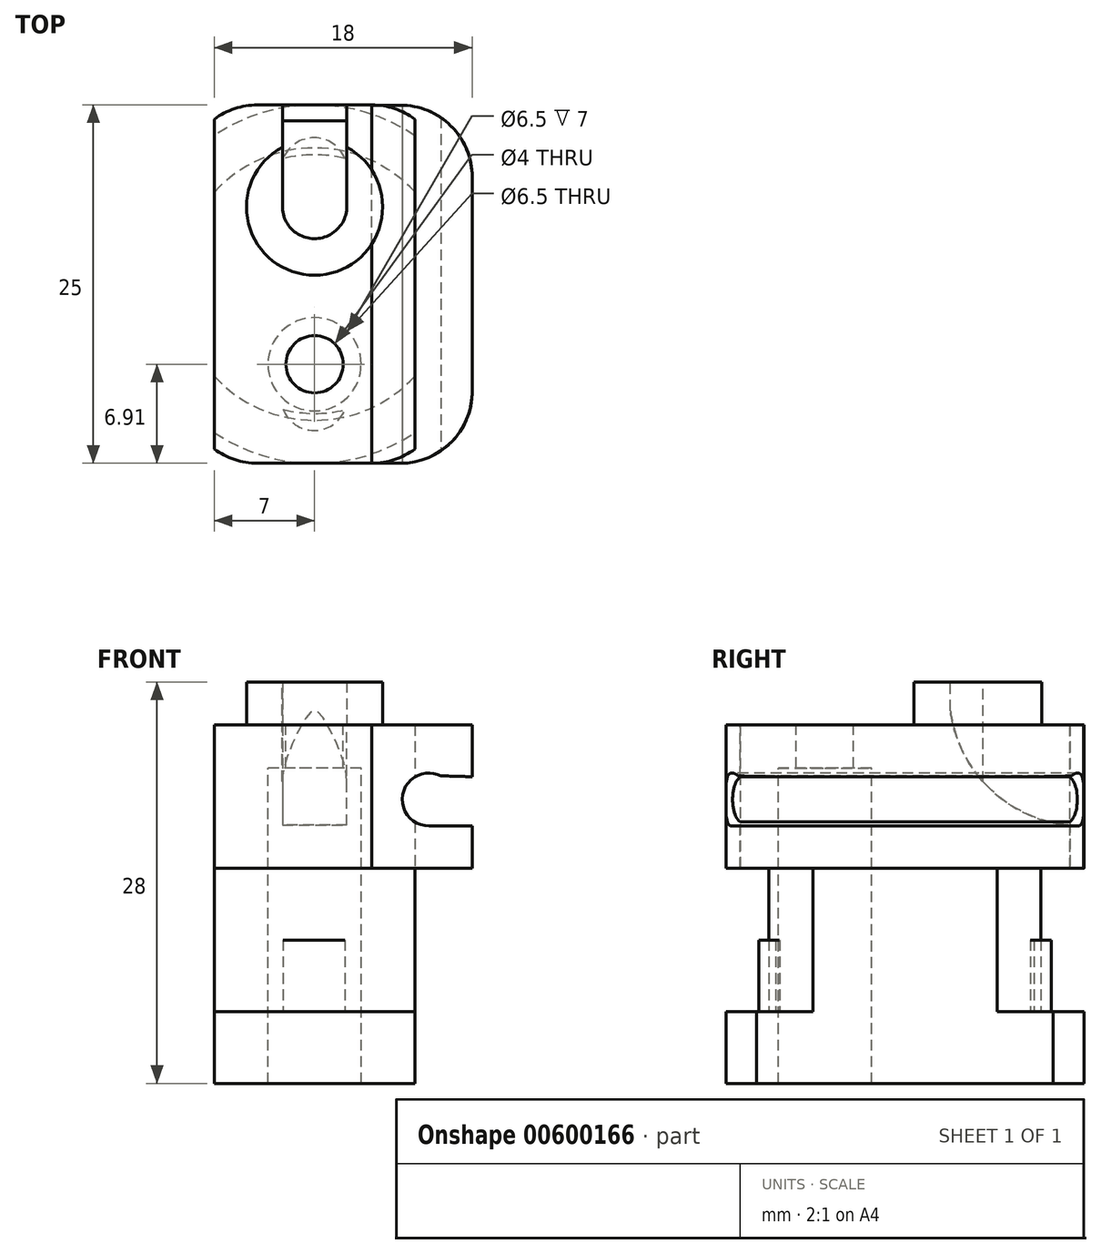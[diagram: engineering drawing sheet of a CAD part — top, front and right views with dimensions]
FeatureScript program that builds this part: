
annotation { "Feature Type Name" : "Feature", "Feature Type Description" : "" }
export const myFeature = defineFeature(function(context is Context, id is Id, definition is map)
    precondition{}
    {
        {
            var Q0;
            Q0=qCreatedBy(makeId("Top.planeOp"),FACE);
            var sketch = newSketch(context, id + "F0", { "sketchPlane" : qUnion([Q0])});
            skCircle(sketch, "E0", {"center": v(0, 0) * mm, "radius": 12.5 * mm});
            skSolve(sketch);
        }
        {
            var Q0;
            Q0=qSketchRegion(id+"F0",true);
            extrude(context, id + "F1", {"entities" : qUnion([Q0]), "oppositeDirection" : true, "depth" : 5 * mm, "offsetDistance" : 25 * mm});
        }
        {
            var Q0;
            Q0=qCreatedBy(makeId("Top.planeOp"),FACE);
            var sketch = newSketch(context, id + "F2", { "sketchPlane" : qUnion([Q0])});
            skCircle(sketch, "E1", {"center": v(0, 0) * mm, "radius": 9.5 * mm});
            skSolve(sketch);
        }
        {
            var Q0;
            Q0=qSketchRegion(id+"F2",true);
            extrude(context, id + "F3", {"entities" : qUnion([Q0]), "operationType" : NewBodyOperationType.ADD, "depth" : 10 * mm, "offsetDistance" : 25 * mm});
        }
        {
            var Q0;
            Q0=qCreatedBy(makeId("Top.planeOp"),FACE);
            var sketch = newSketch(context, id + "F4", { "sketchPlane" : qUnion([Q0])});
            skArc(sketch, "E2", {"start": v(1.01, 8.93) * mm, "mid": v(1, 8.94) * mm, "end": v(1, 8.95) * mm});
            skPoint(sketch, "E3.orphan", {"position": v(0, 9.05) * mm});
            skArc(sketch, "E4", {"start": v(2.13, 8.75) * mm, "mid": v(-0.03, 10.2) * mm, "end": v(-2.2, 8.75) * mm});
            skArc(sketch, "E5", {"start": v(-2.2, 8.75) * mm, "mid": v(-0.03, 9.02) * mm, "end": v(2.13, 8.76) * mm});
            skSolve(sketch);
        }
        {
            var Q0;
            Q0=qSketchRegion(id+"F4",true);
            extrude(context, id + "F5", {"entities" : qUnion([Q0]), "depth" : 5 * mm, "offsetDistance" : 25 * mm});
        }
        {
            var Q0;
            Q0=makeQuery(id+"F5.opExtrude","SWEPT_BODY",BODY,{"disambiguationData":[OSD([sQuery(id+"F4.wireOp",EDGE,"E4"),sQuery(id+"F4.wireOp",EDGE,"E5")])]});
            var Q1;
            Q1=qCreatedBy(makeId("Front.planeOp"),FACE);
            mirror(context, id + "F6", {"entities" : qUnion([Q0]), "mirrorPlane" : qUnion([Q1])});
        }
        {
            var Q0;
            Q0=qCreatedBy(makeId("Top.planeOp"),FACE);
            var sketch = newSketch(context, id + "F7", { "sketchPlane" : qUnion([Q0])});
            skLineSegment(sketch, "E6.bottom", {"start": v(-7.5, -13.5) * mm, "end": v(7.5, -13.5) * mm});
            skLineSegment(sketch, "E6.top", {"start": v(-7.5, 13.5) * mm, "end": v(7.5, 13.5) * mm});
            skLineSegment(sketch, "E6.left", {"start": v(-7.5, -13.5) * mm, "end": v(-7.5, 13.5) * mm});
            skLineSegment(sketch, "E6.right", {"start": v(7.5, -13.5) * mm, "end": v(7.5, 13.5) * mm});
            skPoint(sketch, "E6.middle", {"position": v(0, 0) * mm});
            skLineSegment(sketch, "E7.bottom", {"start": v(-15, -15) * mm, "end": v(15, -15) * mm});
            skLineSegment(sketch, "E7.top", {"start": v(-15, 15) * mm, "end": v(15, 15) * mm});
            skLineSegment(sketch, "E7.left", {"start": v(-15, -15) * mm, "end": v(-15, 15) * mm});
            skLineSegment(sketch, "E7.right", {"start": v(15, -15) * mm, "end": v(15, 15) * mm});
            skSolve(sketch);
        }
        {
            var Q0;
            Q0=qSketchRegion(id+"F7",true);
            extrude(context, id + "F8", {"entities" : qUnion([Q0]), "endBound" : BoundingType.SYMMETRIC, "depth" : 20 * mm, "offsetDistance" : 25 * mm});
        }
        {
            var Q0;
            Q0=makeQuery(id+"F8.opExtrude","SWEPT_BODY",BODY,{"disambiguationData":[OSD([sQuery(id+"F7.wireOp",EDGE,"E6.bottom"),sQuery(id+"F7.wireOp",EDGE,"E6.top"),sQuery(id+"F7.wireOp",EDGE,"E6.left"),sQuery(id+"F7.wireOp",EDGE,"E6.right"),sQuery(id+"F7.wireOp",EDGE,"E7.bottom"),sQuery(id+"F7.wireOp",EDGE,"E7.top"),sQuery(id+"F7.wireOp",EDGE,"E7.left"),sQuery(id+"F7.wireOp",EDGE,"E7.right")])]});
            var Q1;
            Q1=makeQuery(id+"F1.opExtrude","SWEPT_BODY",BODY,{"disambiguationData":[OSD([sQuery(id+"F0.wireOp",EDGE,"E0")])]});
            booleanBodies(context, id + "F9", {"operationType" : BooleanOperationType.SUBTRACTION, "tools" : qUnion([Q0]), "targets" : qUnion([Q1])});
        }
        {
            var Q0;
            Q0=makeQuery(id+"F3.opExtrude","CAP_FACE",FACE,{"disambiguationData":[OSD([sQuery(id+"F2.wireOp",EDGE,"E1")])],"isStart":false});
            var sketch = newSketch(context, id + "F10", { "sketchPlane" : qUnion([Q0])});
            skLineSegment(sketch, "E8.bottom", {"start": v(-9, 12.5) * mm, "end": v(9, 12.5) * mm});
            skLineSegment(sketch, "E8.top", {"start": v(-9, -12.5) * mm, "end": v(9, -12.5) * mm});
            skLineSegment(sketch, "E8.left", {"start": v(-9, 12.5) * mm, "end": v(-9, -12.5) * mm});
            skLineSegment(sketch, "E8.right", {"start": v(9, 12.5) * mm, "end": v(9, -12.5) * mm});
            skPoint(sketch, "E8.middle", {"position": v(0, 0) * mm});
            skSolve(sketch);
        }
        {
            var Q0;
            Q0=qSketchRegion(id+"F10",true);
            extrude(context, id + "F11", {"entities" : qUnion([Q0]), "depth" : 10 * mm, "offsetDistance" : 25 * mm});
        }
        {
            var Q0;
            Q0=makeQuery(id+"F11.opExtrude","SWEPT_EDGE",EDGE,{"disambiguationData":[OSD([sQuery(id+"F10.wireOp",EDGE,"E8.top"),sQuery(id+"F10.wireOp",EDGE,"E8.left")])]});
            var Q1;
            Q1=makeQuery(id+"F11.opExtrude","SWEPT_EDGE",EDGE,{"disambiguationData":[OSD([sQuery(id+"F10.wireOp",EDGE,"E8.top"),sQuery(id+"F10.wireOp",EDGE,"E8.right")])]});
            var Q2;
            Q2=makeQuery(id+"F11.opExtrude","SWEPT_EDGE",EDGE,{"disambiguationData":[OSD([sQuery(id+"F10.wireOp",EDGE,"E8.bottom"),sQuery(id+"F10.wireOp",EDGE,"E8.left")])]});
            var Q3;
            Q3=makeQuery(id+"F11.opExtrude","SWEPT_EDGE",EDGE,{"disambiguationData":[OSD([sQuery(id+"F10.wireOp",EDGE,"E8.bottom"),sQuery(id+"F10.wireOp",EDGE,"E8.right")])]});
            fillet(context, id + "F12", {"entities" : qUnion([Q0, Q1, Q2, Q3]), "radius" : 5 * mm, "tangentPropagation" : true, "allowEdgeOverflow" : false});
        }
        {
            var Q0;
            Q0=makeQuery(id+"F11.opExtrude","CAP_FACE",FACE,{"disambiguationData":[OSD([sQuery(id+"F10.wireOp",EDGE,"E8.bottom"),sQuery(id+"F10.wireOp",EDGE,"E8.top"),sQuery(id+"F10.wireOp",EDGE,"E8.left"),sQuery(id+"F10.wireOp",EDGE,"E8.right")])],"isStart":false});
            var sketch = newSketch(context, id + "F13", { "sketchPlane" : qUnion([Q0])});
            skCircle(sketch, "E9", {"center": v(0, 5.37) * mm, "radius": 4.75 * mm});
            skSolve(sketch);
        }
        {
            var Q0;
            Q0=qSketchRegion(id+"F13",true);
            extrude(context, id + "F14", {"entities" : qUnion([Q0]), "operationType" : NewBodyOperationType.ADD, "depth" : 3 * mm, "offsetDistance" : 25 * mm});
        }
        {
            var Q0;
            Q0=makeQuery(id+"F11.opExtrude","CAP_FACE",FACE,{"disambiguationData":[OSD([sQuery(id+"F10.wireOp",EDGE,"E8.bottom"),sQuery(id+"F10.wireOp",EDGE,"E8.top"),sQuery(id+"F10.wireOp",EDGE,"E8.left"),sQuery(id+"F10.wireOp",EDGE,"E8.right")])],"isStart":false});
            var sketch = newSketch(context, id + "F15", { "sketchPlane" : qUnion([Q0])});
            skLineSegment(sketch, "E10", {"start": v(0, 5.37) * mm, "end": v(0, -5.59) * mm});
            skCircle(sketch, "E11", {"center": v(0, -5.59) * mm, "radius": 2 * mm});
            skSolve(sketch);
        }
        {
            var Q0;
            Q0=qSketchRegion(id+"F15",true);
            extrude(context, id + "F16", {"entities" : qUnion([Q0]), "oppositeDirection" : true, "depth" : 25 * mm, "offsetDistance" : 25 * mm});
        }
        {
            var Q0;
            Q0=makeQuery(id+"F11.opExtrude","CAP_FACE",FACE,{"disambiguationData":[OSD([sQuery(id+"F10.wireOp",EDGE,"E8.bottom"),sQuery(id+"F10.wireOp",EDGE,"E8.top"),sQuery(id+"F10.wireOp",EDGE,"E8.left"),sQuery(id+"F10.wireOp",EDGE,"E8.right")])],"isStart":false});
            cPlane(context, id + "F17", {"entities" : qUnion([Q0]), "cplaneType" : CPlaneType.OFFSET, "offset" : 3 * mm, "oppositeDirection" : true, "width" : 150 * mm, "height" : 150 * mm});
        }
        {
            var Q0;
            Q0=qCreatedBy(id+"F17.planeOp",FACE);
            var sketch = newSketch(context, id + "F18", { "sketchPlane" : qUnion([Q0])});
            skCircle(sketch, "E12", {"center": v(0, -5.59) * mm, "radius": 3.25 * mm});
            skSolve(sketch);
        }
        {
            var Q0;
            Q0=qSketchRegion(id+"F18",true);
            extrude(context, id + "F19", {"entities" : qUnion([Q0]), "oppositeDirection" : true, "depth" : 25 * mm, "offsetDistance" : 25 * mm});
        }
        {
            var Q0;
            Q0=makeQuery(id+"F19.opExtrude","SWEPT_BODY",BODY,{"disambiguationData":[OSD([sQuery(id+"F18.wireOp",EDGE,"E12")])]});
            var Q1;
            Q1=makeQuery(id+"F16.opExtrude","SWEPT_BODY",BODY,{"disambiguationData":[OSD([sQuery(id+"F15.wireOp",EDGE,"E11")])]});
            var Q2;
            Q2=makeQuery(id+"F11.opExtrude","SWEPT_BODY",BODY,{"disambiguationData":[OSD([sQuery(id+"F10.wireOp",EDGE,"E8.bottom"),sQuery(id+"F10.wireOp",EDGE,"E8.top"),sQuery(id+"F10.wireOp",EDGE,"E8.left"),sQuery(id+"F10.wireOp",EDGE,"E8.right")])]});
            var Q3;
            Q3=makeQuery(id+"F1.opExtrude","SWEPT_BODY",BODY,{"disambiguationData":[OSD([sQuery(id+"F0.wireOp",EDGE,"E0")])]});
            booleanBodies(context, id + "F20", {"operationType" : BooleanOperationType.SUBTRACTION, "tools" : qUnion([Q0, Q1]), "targets" : qUnion([Q2, Q3])});
        }
        {
            var Q0;
            Q0=makeQuery(id+"F14.opExtrude","CAP_FACE",FACE,{"disambiguationData":[OSD([sQuery(id+"F13.wireOp",EDGE,"E9")])],"isStart":false});
            var sketch = newSketch(context, id + "F21", { "sketchPlane" : qUnion([Q0])});
            skArc(sketch, "E13", {"start": v(-2.25, 5.46) * mm, "mid": v(-0.02, 3.17) * mm, "end": v(2.25, 5.42) * mm});
            skLineSegment(sketch, "E14", {"start": v(-2.25, 5.38) * mm, "end": v(-2.25, 13.26) * mm});
            skLineSegment(sketch, "E15", {"start": v(-2.25, 13.26) * mm, "end": v(2.25, 13.26) * mm});
            skLineSegment(sketch, "E16", {"start": v(2.25, 13.26) * mm, "end": v(2.25, 5.42) * mm});
            skSolve(sketch);
        }
        {
            var Q0;
            Q0=qSketchRegion(id+"F21",true);
            extrude(context, id + "F22", {"entities" : qUnion([Q0]), "oppositeDirection" : true, "depth" : 10 * mm, "offsetDistance" : 25 * mm});
        }
        {
            var Q0;
            Q0=qCreatedBy(makeId("Right.planeOp"),FACE);
            var sketch = newSketch(context, id + "F23", { "sketchPlane" : qUnion([Q0])});
            skArc(sketch, "E17", {"start": v(3.13, 23.03) * mm, "mid": v(5.2, 16.33) * mm, "end": v(11.38, 13.01) * mm});
            skLineSegment(sketch, "E18", {"start": v(11.38, 13.01) * mm, "end": v(14.3, 13.01) * mm});
            skLineSegment(sketch, "E19", {"start": v(14.3, 13.01) * mm, "end": v(14.3, 22.99) * mm});
            skLineSegment(sketch, "E20", {"start": v(14.3, 22.99) * mm, "end": v(3.13, 23.03) * mm});
            skLineSegment(sketch, "E21.bottom", {"start": v(0.82, 24.72) * mm, "end": v(16.4, 24.72) * mm});
            skLineSegment(sketch, "E21.top", {"start": v(0.82, 11.28) * mm, "end": v(16.4, 11.28) * mm});
            skLineSegment(sketch, "E21.left", {"start": v(0.82, 24.72) * mm, "end": v(0.82, 11.28) * mm});
            skLineSegment(sketch, "E21.right", {"start": v(16.4, 24.72) * mm, "end": v(16.4, 11.28) * mm});
            skSolve(sketch);
        }
        {
            var Q0;
            Q0=qSketchRegion(id+"F23",true);
            extrude(context, id + "F24", {"entities" : qUnion([Q0]), "endBound" : BoundingType.SYMMETRIC, "depth" : 6 * mm, "offsetDistance" : 25 * mm});
        }
        {
            var Q0;
            Q0=makeQuery(id+"F24.opExtrude","SWEPT_BODY",BODY,{"disambiguationData":[OSD([sQuery(id+"F23.wireOp",EDGE,"E17"),sQuery(id+"F23.wireOp",EDGE,"E18"),sQuery(id+"F23.wireOp",EDGE,"E19"),sQuery(id+"F23.wireOp",EDGE,"E20"),sQuery(id+"F23.wireOp",EDGE,"E21.bottom"),sQuery(id+"F23.wireOp",EDGE,"E21.top"),sQuery(id+"F23.wireOp",EDGE,"E21.left"),sQuery(id+"F23.wireOp",EDGE,"E21.right")])]});
            var Q1;
            Q1=makeQuery(id+"F22.opExtrude","SWEPT_BODY",BODY,{"disambiguationData":[OSD([sQuery(id+"F21.wireOp",EDGE,"E13"),sQuery(id+"F21.wireOp",EDGE,"E14"),sQuery(id+"F21.wireOp",EDGE,"E15"),sQuery(id+"F21.wireOp",EDGE,"E16")])]});
            booleanBodies(context, id + "F25", {"operationType" : BooleanOperationType.SUBTRACTION, "tools" : qUnion([Q0]), "targets" : qUnion([Q1])});
        }
        {
            var Q0;
            Q0=makeQuery(id+"F22.opExtrude","SWEPT_BODY",BODY,{"disambiguationData":[OSD([sQuery(id+"F21.wireOp",EDGE,"E13"),sQuery(id+"F21.wireOp",EDGE,"E14"),sQuery(id+"F21.wireOp",EDGE,"E15"),sQuery(id+"F21.wireOp",EDGE,"E16")])]});
            var Q1;
            Q1=makeQuery(id+"F11.opExtrude","SWEPT_BODY",BODY,{"disambiguationData":[OSD([sQuery(id+"F10.wireOp",EDGE,"E8.bottom"),sQuery(id+"F10.wireOp",EDGE,"E8.top"),sQuery(id+"F10.wireOp",EDGE,"E8.left"),sQuery(id+"F10.wireOp",EDGE,"E8.right")])]});
            booleanBodies(context, id + "F26", {"operationType" : BooleanOperationType.SUBTRACTION, "tools" : qUnion([Q0]), "targets" : qUnion([Q1])});
        }
        {
            var Q0;
            Q0=qCreatedBy(makeId("Top.planeOp"),FACE);
            var sketch = newSketch(context, id + "F27", { "sketchPlane" : qUnion([Q0])});
            skLineSegment(sketch, "E22", {"start": v(4.98, 9.1) * mm, "end": v(4.98, -15.76) * mm});
            skLineSegment(sketch, "E23", {"start": v(4.98, 9.1) * mm, "end": v(4.98, 13.82) * mm});
            skSolve(sketch);
        }
        {
            var Q0;
            Q0=qCreatedBy(makeId("Front.planeOp"),FACE);
            var sketch = newSketch(context, id + "F28", { "sketchPlane" : qUnion([Q0])});
            skArc(sketch, "E24", {"start": v(8.81, 16.45) * mm, "mid": v(6.17, 15.23) * mm, "end": v(7.98, 12.95) * mm});
            skLineSegment(sketch, "E25", {"start": v(8.81, 16.45) * mm, "end": v(12.25, 16.36) * mm});
            skLineSegment(sketch, "E26", {"start": v(12.25, 16.36) * mm, "end": v(12.25, 12.98) * mm});
            skLineSegment(sketch, "E27", {"start": v(12.25, 12.98) * mm, "end": v(7.98, 12.95) * mm});
            skSolve(sketch);
        }
        {
            var Q0;
            Q0=makeQuery(id+"F1.opExtrude","CAP_FACE",FACE,{"disambiguationData":[OSD([sQuery(id+"F0.wireOp",EDGE,"E0")])],"isStart":false});
            var sketch = newSketch(context, id + "F29", { "sketchPlane" : qUnion([Q0])});
            skLineSegment(sketch, "E28.bottom", {"start": v(-7, 13.5) * mm, "end": v(7, 13.5) * mm});
            skLineSegment(sketch, "E28.top", {"start": v(-7, -13.5) * mm, "end": v(7, -13.5) * mm});
            skLineSegment(sketch, "E28.left", {"start": v(-7, 13.5) * mm, "end": v(-7, -13.5) * mm});
            skLineSegment(sketch, "E28.right", {"start": v(7, 13.5) * mm, "end": v(7, -13.5) * mm});
            skPoint(sketch, "E28.middle", {"position": v(0, 0) * mm});
            skLineSegment(sketch, "E29.bottom", {"start": v(-10.65, 16.44) * mm, "end": v(10.65, 16.44) * mm});
            skLineSegment(sketch, "E29.top", {"start": v(-10.65, -16.44) * mm, "end": v(10.65, -16.44) * mm});
            skLineSegment(sketch, "E29.left", {"start": v(-10.65, 16.44) * mm, "end": v(-10.65, -16.44) * mm});
            skLineSegment(sketch, "E29.right", {"start": v(10.65, 16.44) * mm, "end": v(10.65, -16.44) * mm});
            skSolve(sketch);
        }
        {
            var Q0;
            {var subQ1=sQuery(id+"F0.wireOp",EDGE,"E0");var subQ7=makeQuery(id+"F9.opBoolean","INTERSECT",EDGE,{"derivedFrom":[makeQuery(id+"F1.opExtrude","CAP_FACE",FACE,{"disambiguationData":[OSD([subQ1])],"isStart":false}),makeQuery(id+"F8.opExtrude","SWEPT_FACE",FACE,{"disambiguationData":[OSD([sQuery(id+"F7.wireOp",EDGE,"E6.left")])]})]});Q0=makeQuery(id+"F29.imprint","IMPRINT",FACE,{"disambiguationData":[TD([[makeQuery(id+"F29.imprint","IMPRINT",EDGE,{"derivedFrom":subQ7}),-1.0]])]});}
            var Q1;
            {var subQ1=sQuery(id+"F0.wireOp",EDGE,"E0");var subQ7=makeQuery(id+"F9.opBoolean","INTERSECT",EDGE,{"derivedFrom":[makeQuery(id+"F1.opExtrude","CAP_FACE",FACE,{"disambiguationData":[OSD([subQ1])],"isStart":false}),makeQuery(id+"F8.opExtrude","SWEPT_FACE",FACE,{"disambiguationData":[OSD([sQuery(id+"F7.wireOp",EDGE,"E6.right")])]})]});Q1=makeQuery(id+"F29.imprint","IMPRINT",FACE,{"disambiguationData":[TD([[makeQuery(id+"F29.imprint","IMPRINT",EDGE,{"derivedFrom":subQ7}),1.0]])]});}
            var Q2;
            {var subQ6=sQuery(id+"F29.wireOp",EDGE,"E28.bottom");Q2=makeQuery(id+"F29.imprint","IMPRINT",FACE,{"disambiguationData":[TD([[makeQuery(id+"F29.imprint","IMPRINT",EDGE,{"derivedFrom":subQ6}),1.0]])]});}
            extrude(context, id + "F30", {"entities" : qUnion([Q0, Q1, Q2]), "oppositeDirection" : true, "depth" : 35 * mm, "offsetDistance" : 25 * mm});
        }
        {
            var Q0;
            Q0=makeQuery(id+"F30.opExtrude","SWEPT_BODY",BODY,{"disambiguationData":[OSD([sQuery(id+"F29.wireOp",EDGE,"E28.bottom"),sQuery(id+"F29.wireOp",EDGE,"E28.top"),sQuery(id+"F29.wireOp",EDGE,"E28.left"),sQuery(id+"F29.wireOp",EDGE,"E28.right"),sQuery(id+"F29.wireOp",EDGE,"E29.bottom"),sQuery(id+"F29.wireOp",EDGE,"E29.top"),sQuery(id+"F29.wireOp",EDGE,"E29.left"),sQuery(id+"F29.wireOp",EDGE,"E29.right")])]});
            var Q1;
            Q1=makeQuery(id+"F11.opExtrude","SWEPT_BODY",BODY,{"disambiguationData":[OSD([sQuery(id+"F10.wireOp",EDGE,"E8.bottom"),sQuery(id+"F10.wireOp",EDGE,"E8.top"),sQuery(id+"F10.wireOp",EDGE,"E8.left"),sQuery(id+"F10.wireOp",EDGE,"E8.right")])]});
            var Q2;
            Q2=makeQuery(id+"F6.opPattern","COPY",BODY,{"derivedFrom":makeQuery(id+"F5.opExtrude","SWEPT_BODY",BODY,{"disambiguationData":[OSD([sQuery(id+"F4.wireOp",EDGE,"E4"),sQuery(id+"F4.wireOp",EDGE,"E5")])]}),"instanceName":"1"});
            var Q3;
            Q3=makeQuery(id+"F5.opExtrude","SWEPT_BODY",BODY,{"disambiguationData":[OSD([sQuery(id+"F4.wireOp",EDGE,"E4"),sQuery(id+"F4.wireOp",EDGE,"E5")])]});
            var Q4;
            Q4=makeQuery(id+"F1.opExtrude","SWEPT_BODY",BODY,{"disambiguationData":[OSD([sQuery(id+"F0.wireOp",EDGE,"E0")])]});
            booleanBodies(context, id + "F31", {"operationType" : BooleanOperationType.SUBTRACTION, "tools" : qUnion([Q0]), "targets" : qUnion([Q1, Q2, Q3, Q4])});
        }
        {
            var Q0;
            Q0=makeQuery(id+"F11.opExtrude","CAP_FACE",FACE,{"disambiguationData":[OSD([sQuery(id+"F10.wireOp",EDGE,"E8.bottom"),sQuery(id+"F10.wireOp",EDGE,"E8.top"),sQuery(id+"F10.wireOp",EDGE,"E8.left"),sQuery(id+"F10.wireOp",EDGE,"E8.right")])],"isStart":true});
            var sketch = newSketch(context, id + "F32", { "sketchPlane" : qUnion([Q0])});
            skLineSegment(sketch, "E30.left", {"start": v(4, 12.5) * mm, "end": v(4, -12.47) * mm});
            skLineSegment(sketch, "E31", {"start": v(4, 12.5) * mm, "end": v(11, 12.5) * mm});
            skLineSegment(sketch, "E32", {"start": v(11, 12.5) * mm, "end": v(11, -12.5) * mm});
            skLineSegment(sketch, "E33", {"start": v(11, -12.5) * mm, "end": v(4, -12.47) * mm});
            skSolve(sketch);
        }
        {
            var Q0;
            Q0=qSketchRegion(id+"F32",true);
            extrude(context, id + "F33", {"entities" : qUnion([Q0]), "oppositeDirection" : true, "depth" : 10 * mm, "offsetDistance" : 25 * mm});
        }
        {
            var Q0;
            Q0=makeQuery(id+"F33.opExtrude","SWEPT_EDGE",EDGE,{"disambiguationData":[OSD([sQuery(id+"F32.wireOp",EDGE,"E32"),sQuery(id+"F32.wireOp",EDGE,"E33")])]});
            var Q1;
            Q1=makeQuery(id+"F33.opExtrude","SWEPT_EDGE",EDGE,{"disambiguationData":[OSD([sQuery(id+"F32.wireOp",EDGE,"E31"),sQuery(id+"F32.wireOp",EDGE,"E32")])]});
            fillet(context, id + "F34", {"entities" : qUnion([Q0, Q1]), "radius" : 5 * mm, "tangentPropagation" : true, "allowEdgeOverflow" : false});
        }
        {
            var Q0;
            Q0=qSketchRegion(id+"F28",true);
            var Q1;
            Q1=qConstructionFilter(qBodyType(qCreatedBy(id+"F27",EDGE),BodyType.WIRE),ConstructionObject.NO);
            sweep(context, id + "F35", {"profiles" : qUnion([Q0]), "path" : qUnion([Q1])});
        }
        {
            var Q0;
            Q0=makeQuery(id+"F35.opSweep","SWEPT_BODY",BODY,{"disambiguationData":[OSD([sQuery(id+"F27.wireOp",EDGE,"E23"),sQuery(id+"F28.wireOp",EDGE,"E24"),sQuery(id+"F28.wireOp",EDGE,"E25"),sQuery(id+"F28.wireOp",EDGE,"E26"),sQuery(id+"F28.wireOp",EDGE,"E27")])]});
            var Q1;
            Q1=makeQuery(id+"F11.opExtrude","SWEPT_BODY",BODY,{"disambiguationData":[OSD([sQuery(id+"F10.wireOp",EDGE,"E8.bottom"),sQuery(id+"F10.wireOp",EDGE,"E8.top"),sQuery(id+"F10.wireOp",EDGE,"E8.left"),sQuery(id+"F10.wireOp",EDGE,"E8.right")])]});
            var Q2;
            Q2=makeQuery(id+"F33.opExtrude","SWEPT_BODY",BODY,{"disambiguationData":[OSD([sQuery(id+"F32.wireOp",EDGE,"E30.left"),sQuery(id+"F32.wireOp",EDGE,"E31"),sQuery(id+"F32.wireOp",EDGE,"E32"),sQuery(id+"F32.wireOp",EDGE,"E33")])]});
            booleanBodies(context, id + "F36", {"operationType" : BooleanOperationType.SUBTRACTION, "tools" : qUnion([Q0]), "targets" : qUnion([Q1, Q2])});
        }
    });
